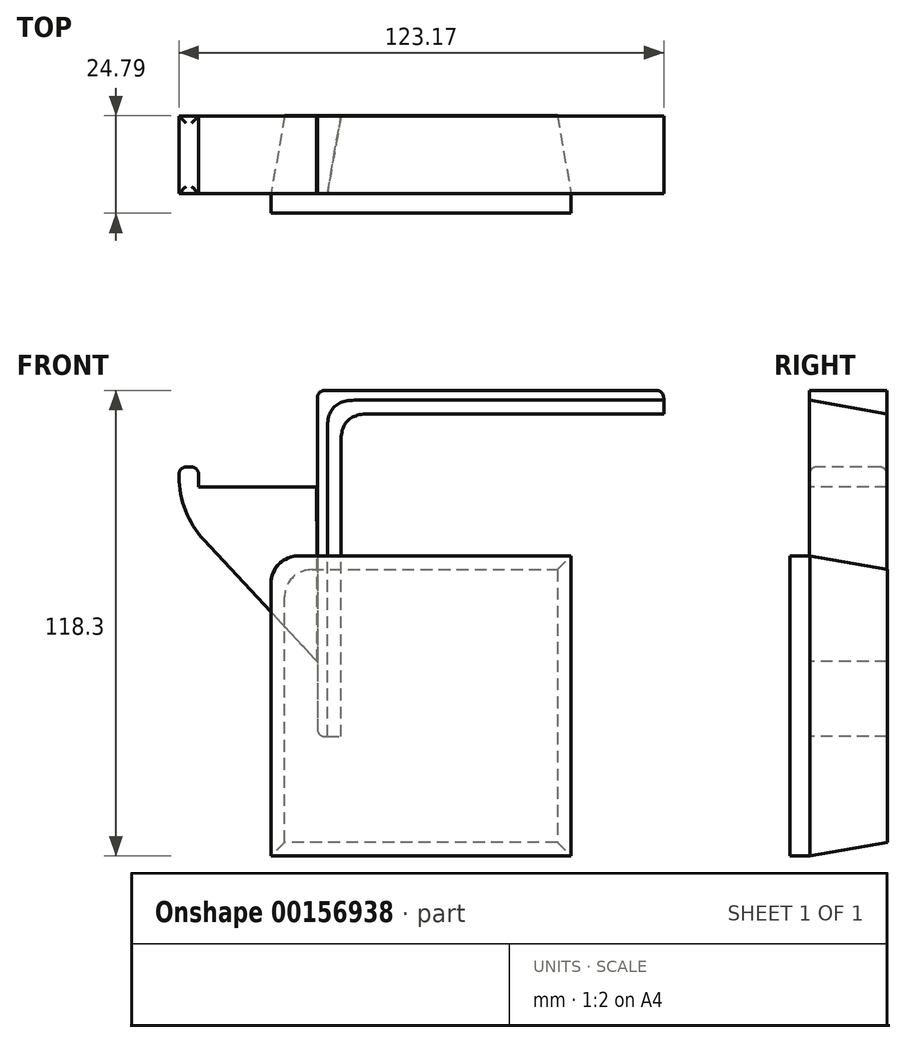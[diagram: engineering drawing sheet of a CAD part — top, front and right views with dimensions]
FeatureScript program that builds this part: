
annotation { "Feature Type Name" : "Feature", "Feature Type Description" : "" }
export const myFeature = defineFeature(function(context is Context, id is Id, definition is map)
    precondition{}
    {
        {
            var Q0;
            Q0=qCreatedBy(makeId("Front.planeOp"),FACE);
            var sketch = newSketch(context, id + "F0", { "sketchPlane" : qUnion([Q0])});
            skLineSegment(sketch, "E0.bottom", {"start": v(38.1, 38.1) * mm, "end": v(-38.1, 38.1) * mm});
            skLineSegment(sketch, "E0.top", {"start": v(38.1, -38.1) * mm, "end": v(-38.1, -38.1) * mm});
            skLineSegment(sketch, "E0.left", {"start": v(38.1, 38.1) * mm, "end": v(38.1, -38.1) * mm});
            skLineSegment(sketch, "E0.right", {"start": v(-38.1, 38.1) * mm, "end": v(-38.1, -38.1) * mm});
            skPoint(sketch, "E0.middle", {"position": v(0, 0) * mm});
            skSolve(sketch);
        }
        {
            var Q0;
            Q0 = qSketchRegion(id + "F0", true);
            extrude(context, id + "F1", {"entities" : qUnion([Q0]), "depth" : 5 * mm});
        }
        {
            var Q0;
            Q0=makeQuery(id+"F1.opExtrude","SWEPT_EDGE",EDGE,{"disambiguationData":[OSD([sQuery(id+"F0.wireOp",EDGE,"E0.bottom"),sQuery(id+"F0.wireOp",EDGE,"E0.right")])]});
            fillet(context, id + "F2", {"entities" : qUnion([Q0]), "radius" : 7 * mm, "tangentPropagation" : true, "allowEdgeOverflow" : false});
        }
        {
            var Q0;
            Q0=makeQuery(id+"F0.imprint","IMPRINT",FACE,{"disambiguationData":[TD([[makeQuery(id+"F0.imprint","IMPRINT",EDGE,{"derivedFrom":sQuery(id+"F0.wireOp",EDGE,"E0.bottom")}),1.0]])]});
            extrude(context, id + "F3", {"entities" : qUnion([Q0]), "operationType" : NewBodyOperationType.ADD, "oppositeDirection" : true, "depth" : 19.79 * mm});
        }
        {
            var Q0;
            Q0=makeQuery(id+"F3.opExtrude","CAP_FACE",FACE,{"disambiguationData":[OSD([sQuery(id+"F0.wireOp",EDGE,"E0.bottom"),sQuery(id+"F0.wireOp",EDGE,"E0.top"),sQuery(id+"F0.wireOp",EDGE,"E0.left"),sQuery(id+"F0.wireOp",EDGE,"E0.right")])],"isStart":false});
            chamfer(context, id + "F4", {"entities" : qUnion([Q0]), "chamferType" : ChamferType.OFFSET_ANGLE, "width" : 19.7 * mm, "oppositeDirection" : false, "angle" : 10 * degree, "tangentPropagation" : true});
        }
        {
            var Q0;
            Q0=makeQuery(id+"F4.opChamfer","BLEND_EDGE",EDGE,{"blendedFrom":[makeQuery(id+"F3.opExtrude","CAP_EDGE",EDGE,{"disambiguationData":[OSD([sQuery(id+"F0.wireOp",EDGE,"E0.bottom")])],"isStart":false}),makeQuery(id+"F3.opExtrude","CAP_EDGE",EDGE,{"disambiguationData":[OSD([sQuery(id+"F0.wireOp",EDGE,"E0.right")])],"isStart":false})],"blendedInto":[]});
            fillet(context, id + "F5", {"entities" : qUnion([Q0]), "radius" : 7 * mm, "tangentPropagation" : true, "allowEdgeOverflow" : false});
        }
        {
            var Q0;
            Q0=qCreatedBy(makeId("Front.planeOp"),FACE);
            var sketch = newSketch(context, id + "F6", { "sketchPlane" : qUnion([Q0])});
            skLineSegment(sketch, "E1", {"start": v(-26.33, -7.8) * mm, "end": v(-20.33, -7.8) * mm});
            skLineSegment(sketch, "E2", {"start": v(-20.33, -7.8) * mm, "end": v(-20.33, 74.2) * mm});
            skLineSegment(sketch, "E3", {"start": v(-20.33, 74.2) * mm, "end": v(61.67, 74.2) * mm});
            skLineSegment(sketch, "E4", {"start": v(61.67, 74.2) * mm, "end": v(61.67, 80.2) * mm});
            skLineSegment(sketch, "E5", {"start": v(61.67, 80.2) * mm, "end": v(-26.33, 80.2) * mm});
            skLineSegment(sketch, "E6", {"start": v(-26.33, 80.2) * mm, "end": v(-26.33, -7.8) * mm});
            skSolve(sketch);
        }
        {
            var Q0;
            Q0=makeQuery(id+"F6.imprint","IMPRINT",FACE,{"disambiguationData":[TD([[makeQuery(id+"F6.imprint","IMPRINT",EDGE,{"derivedFrom":sQuery(id+"F6.wireOp",EDGE,"E1")}),1.0]])]});
            extrude(context, id + "F7", {"entities" : qUnion([Q0]), "oppositeDirection" : true, "depth" : 19.7 * mm});
        }
        {
            var Q0;
            Q0=makeQuery(id+"F7.opExtrude","CAP_EDGE",EDGE,{"disambiguationData":[OSD([sQuery(id+"F6.wireOp",EDGE,"E2")])],"isStart":true});
            var Q1;
            Q1=makeQuery(id+"F7.opExtrude","CAP_EDGE",EDGE,{"disambiguationData":[OSD([sQuery(id+"F6.wireOp",EDGE,"E3")])],"isStart":true});
            chamfer(context, id + "F8", {"entities" : qUnion([Q0, Q1]), "chamferType" : ChamferType.OFFSET_ANGLE, "width" : 19.7 * mm, "oppositeDirection" : true, "angle" : 10 * degree, "tangentPropagation" : true});
        }
        {
            var Q0;
            Q0=makeQuery(id+"F8.opChamfer","BLEND_EDGE",EDGE,{"blendedFrom":[makeQuery(id+"F7.opExtrude","CAP_EDGE",EDGE,{"disambiguationData":[OSD([sQuery(id+"F6.wireOp",EDGE,"E2")])],"isStart":true}),makeQuery(id+"F7.opExtrude","CAP_EDGE",EDGE,{"disambiguationData":[OSD([sQuery(id+"F6.wireOp",EDGE,"E3")])],"isStart":true})],"blendedInto":[]});
            fillet(context, id + "F9", {"entities" : qUnion([Q0]), "radius" : 7 * mm, "tangentPropagation" : true, "rho" : 0.5, "crossSection" : FilletCrossSection.CONIC, "allowEdgeOverflow" : false});
        }
        {
            var Q0;
            Q0=qCreatedBy(makeId("Front.planeOp"),FACE);
            var sketch = newSketch(context, id + "F10", { "sketchPlane" : qUnion([Q0])});
            skLineSegment(sketch, "E7", {"start": v(-26.5, 55.7) * mm, "end": v(-56.5, 55.7) * mm});
            skLineSegment(sketch, "E8", {"start": v(-56.5, 55.7) * mm, "end": v(-56.5, 60.7) * mm});
            skLineSegment(sketch, "E9", {"start": v(-56.5, 60.7) * mm, "end": v(-61.5, 60.7) * mm});
            skLineSegment(sketch, "E10", {"start": v(-61.5, 60.7) * mm, "end": v(-61.5, 49) * mm});
            skLineSegment(sketch, "E11", {"start": v(-61.5, 49) * mm, "end": v(-26.43, 11.32) * mm});
            skLineSegment(sketch, "E12", {"start": v(-26.43, 11.32) * mm, "end": v(-26.5, 55.7) * mm});
            skSolve(sketch);
        }
        {
            var Q0;
            Q0=makeQuery(id+"F10.imprint","IMPRINT",FACE,{"disambiguationData":[TD([[makeQuery(id+"F10.imprint","IMPRINT",EDGE,{"derivedFrom":sQuery(id+"F10.wireOp",EDGE,"E7")}),1.0]])]});
            extrude(context, id + "F11", {"entities" : qUnion([Q0]), "oppositeDirection" : true, "depth" : 19.7 * mm});
        }
        {
            var Q0;
            Q0=makeQuery(id+"F11.opExtrude","SWEPT_FACE",FACE,{"disambiguationData":[OSD([sQuery(id+"F10.wireOp",EDGE,"E9")])]});
            fillet(context, id + "F12", {"entities" : qUnion([Q0]), "radius" : 1.81 * mm, "tangentPropagation" : true, "allowEdgeOverflow" : false});
        }
        {
            var Q0;
            Q0=makeQuery(id+"F11.opExtrude","SWEPT_EDGE",EDGE,{"disambiguationData":[OSD([sQuery(id+"F10.wireOp",EDGE,"E10"),sQuery(id+"F10.wireOp",EDGE,"E11")])]});
            fillet(context, id + "F13", {"entities" : qUnion([Q0]), "radius" : 23.46 * mm, "tangentPropagation" : true, "allowEdgeOverflow" : false});
        }
        {
            var Q0;
            Q0=makeQuery(id+"F7.opExtrude","SWEPT_EDGE",EDGE,{"disambiguationData":[OSD([sQuery(id+"F6.wireOp",EDGE,"E5"),sQuery(id+"F6.wireOp",EDGE,"E6")])]});
            fillet(context, id + "F14", {"entities" : qUnion([Q0]), "radius" : 2 * mm, "tangentPropagation" : true, "allowEdgeOverflow" : false});
        }
        {
            var Q0;
            Q0=makeQuery(id+"F7.opExtrude","SWEPT_EDGE",EDGE,{"disambiguationData":[OSD([sQuery(id+"F6.wireOp",EDGE,"E1"),sQuery(id+"F6.wireOp",EDGE,"E6")])]});
            fillet(context, id + "F15", {"entities" : qUnion([Q0]), "radius" : 2 * mm, "tangentPropagation" : true, "allowEdgeOverflow" : false});
        }
        {
            var Q0;
            Q0=makeQuery(id+"F7.opExtrude","SWEPT_EDGE",EDGE,{"disambiguationData":[OSD([sQuery(id+"F6.wireOp",EDGE,"E4"),sQuery(id+"F6.wireOp",EDGE,"E5")])]});
            fillet(context, id + "F16", {"entities" : qUnion([Q0]), "radius" : 2 * mm, "tangentPropagation" : true, "allowEdgeOverflow" : false});
        }
    });
